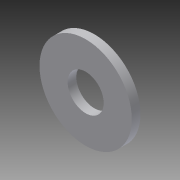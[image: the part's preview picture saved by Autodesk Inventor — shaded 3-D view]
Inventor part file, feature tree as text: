
AUTODESK INVENTOR PART (.ipt)
format: ipt  version: 2014 (Build 180170000, 170)  size: 76,288 bytes
history: native  units: in
note: dims shown in document units (in); Inventor stores cm internally (conversion verified against a paired STEP export)
features: extrude x1, sketch x1
ambient origin geometry x8: Origin, YZ Plane, XZ Plane, XY Plane, X Axis, Y Axis, Z Axis, Center Point
bodies: Solid1 (feature_tree)
feature tree (2):
  extrude  "Extrusion1"  Depth=0.03in
  sketch  "Sketch1"  dims[d0=0.125in d1=0.32in d2=0.03in d3=0.0in]
